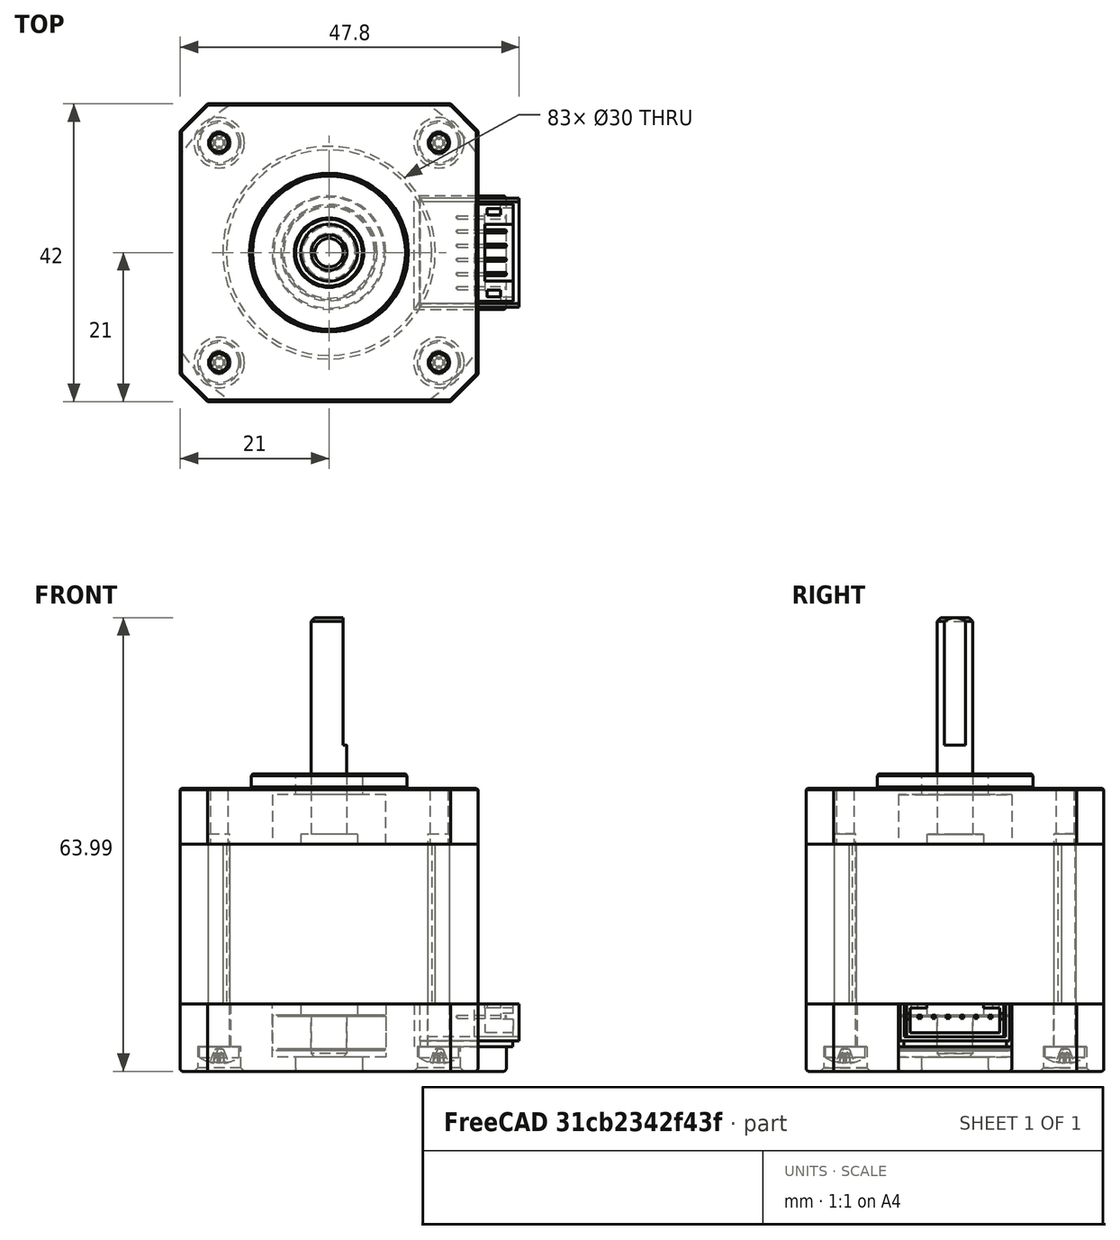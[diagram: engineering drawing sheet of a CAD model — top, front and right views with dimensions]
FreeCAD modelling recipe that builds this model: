
FCSTD DOCUMENT  (FreeCAD 0.18R16131 (Git))
Label: Nema_17-17HS4401
License: CreativeCommons Attribution
LicenseURL: http://creativecommons.org/licenses/by/4.0/
objects: Sketcher::SketchObject×21, PartDesign::Body×10, PartDesign::Pocket×10, PartDesign::Pad×8, Part::FeaturePython×5, PartDesign::Chamfer×3, PartDesign::Revolution×2, PartDesign::LinearPattern×1, PartDesign::Hole×1, PartDesign::Fillet×1, PartDesign::FeatureBase×1, App::Part×1
note: 84 computed .brp shape members not serialized (recipe doc carries the construction recipe); baked Part::Feature solids carry a one-line shape summary decoded from their .brp

FEATURE [Sketcher::SketchObject] Sketch
  MapMode = 5
  Support = -> [XY_Plane]
  sketch-geometry (1):
    g0: Circle CenterX=0 CenterY=0 CenterZ=0 NormalX=0 NormalY=0 NormalZ=1 AngleXU=0 Radius=11
  constraints (2):
    c: Coincident(g0,g-1)
    c: Diameter(g0) = 22
FEATURE [PartDesign::Pad] Pad
  Length = 2
  Length2 = 100
  Profile = -> Sketch
  Type = 0
FEATURE [Sketcher::SketchObject] Sketch001
  MapMode = 5
  Support = -> [XY_Plane]
  sketch-geometry (8):
    g0: LineSegment StartX=-21 StartY=17.15 StartZ=0 EndX=-21 EndY=-17.15 EndZ=0
    g1: LineSegment StartX=-21 StartY=-17.15 StartZ=0 EndX=-17.15 EndY=-21 EndZ=0
    g2: LineSegment StartX=-17.15 StartY=-21 StartZ=0 EndX=17.15 EndY=-21 EndZ=0
    g3: LineSegment StartX=17.15 StartY=-21 StartZ=0 EndX=21 EndY=-17.15 EndZ=0
    g4: LineSegment StartX=21 StartY=-17.15 StartZ=0 EndX=21 EndY=17.15 EndZ=0
    g5: LineSegment StartX=21 StartY=17.15 StartZ=0 EndX=17.15 EndY=21 EndZ=0
    g6: LineSegment StartX=17.15 StartY=21 StartZ=0 EndX=-17.15 EndY=21 EndZ=0
    g7: LineSegment StartX=-17.15 StartY=21 StartZ=0 EndX=-21 EndY=17.15 EndZ=0
  constraints (21):
    c: Coincident(g0,g1)
    c: Coincident(g1,g2)
    c: Coincident(g2,g3)
    c: Coincident(g3,g4)
    c: Coincident(g4,g5)
    c: Coincident(g5,g6)
    c: Coincident(g6,g7)
    c: Coincident(g7,g0)
    c: Symmetric(g1,g2,g-2)
    c: Symmetric(g0,g0,g-1)
    c: Equal(g7,g5)
    c: Equal(g5,g3)
    c: Equal(g3,g1)
    c: Equal(g0,g6)
    c: Equal(g6,g4)
    c: Equal(g4,g2)
    c: Symmetric(g6,g5,g-2)
    c: Symmetric(g4,g3,g-1)
    c: Perpendicular(g7,g1)
    c: DistanceX(g0,g4) = 42
    c: DistanceY(g2,g3) = 3.85
FEATURE [PartDesign::Pad] Pad001
  BaseFeature = -> Pad
  Length = 7.9
  Length2 = 100
  Profile = -> Sketch001
  Reversed = true
  Type = 0
FEATURE [Sketcher::SketchObject] Sketch003
  MapMode = 5
  Support = -> [XY_Plane]
  sketch-geometry (8):
    g0: LineSegment [constr] StartX=-15.5 StartY=15.5 StartZ=0 EndX=15.5 EndY=15.5 EndZ=0
    g1: LineSegment [constr] StartX=15.5 StartY=15.5 StartZ=0 EndX=15.5 EndY=-15.5 EndZ=0
    g2: LineSegment [constr] StartX=15.5 StartY=-15.5 StartZ=0 EndX=-15.5 EndY=-15.5 EndZ=0
    g3: LineSegment [constr] StartX=-15.5 StartY=-15.5 StartZ=0 EndX=-15.5 EndY=15.5 EndZ=0
    g4: Circle CenterX=-15.5 CenterY=15.5 CenterZ=0 NormalX=0 NormalY=0 NormalZ=1 AngleXU=0 Radius=1.25
    g5: Circle CenterX=15.5 CenterY=15.5 CenterZ=0 NormalX=0 NormalY=0 NormalZ=1 AngleXU=0 Radius=1.25
    g6: Circle CenterX=15.5 CenterY=-15.5 CenterZ=0 NormalX=0 NormalY=0 NormalZ=1 AngleXU=0 Radius=1.25
    g7: Circle CenterX=-15.5 CenterY=-15.5 CenterZ=0 NormalX=0 NormalY=0 NormalZ=1 AngleXU=0 Radius=1.25
  constraints (19):
    c: Coincident(g0,g1)
    c: Coincident(g1,g2)
    c: Coincident(g2,g3)
    c: Coincident(g3,g0)
    c: Horizontal(g0)
    c: Horizontal(g2)
    c: Vertical(g1)
    c: Vertical(g3)
    c: Equal(g3,g0)
    c: Symmetric(g2,g0,g-1)
    c: Coincident(g4,g0)
    c: Coincident(g5,g0)
    c: Coincident(g6,g1)
    c: Coincident(g7,g2)
    c: Equal(g4,g5)
    c: Equal(g5,g6)
    c: Equal(g6,g7)
    c: Diameter(g4) = 2.5
    c: DistanceY(g1,g1) = 31
FEATURE [Sketcher::SketchObject] Sketch004
  AttachmentOffset = pos=(0,0,-7.9) rot=(1,0,0;3.14159rad)
  MapMode = 5
  Placement = pos=(0,0,-7.9) rot=(1,0,0;3.14159rad)
  Support = -> [XY_Plane]
  expr: AttachmentOffset.Base.z = -Pad001.Length
  sketch-geometry (1):
    g0: Circle CenterX=0 CenterY=0 CenterZ=0 NormalX=0 NormalY=0 NormalZ=1 AngleXU=0 Radius=8
  constraints (2):
    c: Coincident(g0,g-1)
    c: Diameter(g0) = 16
FEATURE [Sketcher::SketchObject] Sketch005
  MapMode = 5
  Support = -> [XY_Plane001]
  sketch-geometry (25):
    g0: LineSegment StartX=-13.1381 StartY=21 StartZ=0 EndX=13.1381 EndY=21 EndZ=0
    g1: LineSegment StartX=21 StartY=13.1381 StartZ=0 EndX=21 EndY=-13.1381 EndZ=0
    g2: LineSegment StartX=13.1381 StartY=-21 StartZ=0 EndX=-13.1381 EndY=-21 EndZ=0
    g3: LineSegment StartX=-21 StartY=-13.1381 StartZ=0 EndX=-21 EndY=13.1381 EndZ=0
    g4: ArcOfCircle CenterX=-2e-16 CenterY=0 CenterZ=0 NormalX=0 NormalY=0 NormalZ=1 AngleXU=0 Radius=25.1 StartAngle=2.17578 EndAngle=2.53661
    g5: ArcOfCircle CenterX=-2e-16 CenterY=0 CenterZ=0 NormalX=0 NormalY=0 NormalZ=1 AngleXU=0 Radius=25.1 StartAngle=0.604985 EndAngle=0.965812
    g6: ArcOfCircle CenterX=-2e-16 CenterY=0 CenterZ=0 NormalX=0 NormalY=0 NormalZ=1 AngleXU=0 Radius=25.1 StartAngle=3.74658 EndAngle=4.1074
    g7: ArcOfCircle CenterX=-2e-16 CenterY=0 CenterZ=0 NormalX=0 NormalY=0 NormalZ=1 AngleXU=0 Radius=25.1 StartAngle=5.31737 EndAngle=5.6782
    g8: ArcOfCircle CenterX=-13.1381 CenterY=19 CenterZ=0 NormalX=0 NormalY=0 NormalZ=1 AngleXU=0 Radius=2 StartAngle=1.5708 EndAngle=2.17578
    g9: ArcOfCircle CenterX=13.1381 CenterY=19 CenterZ=0 NormalX=0 NormalY=0 NormalZ=1 AngleXU=0 Radius=2 StartAngle=0.965812 EndAngle=1.5708
    g10: ArcOfCircle CenterX=19 CenterY=13.1381 CenterZ=0 NormalX=0 NormalY=0 NormalZ=1 AngleXU=0 Radius=2 StartAngle=0 EndAngle=0.604985
    g11: ArcOfCircle CenterX=-19 CenterY=13.1381 CenterZ=0 NormalX=0 NormalY=0 NormalZ=1 AngleXU=0 Radius=2 StartAngle=2.53661 EndAngle=3.14159
    g12: ArcOfCircle CenterX=-19 CenterY=-13.1381 CenterZ=0 NormalX=0 NormalY=0 NormalZ=1 AngleXU=0 Radius=2 StartAngle=3.14159 EndAngle=3.74658
    g13: ArcOfCircle CenterX=-13.1381 CenterY=-19 CenterZ=0 NormalX=0 NormalY=0 NormalZ=1 AngleXU=0 Radius=2 StartAngle=4.1074 EndAngle=4.71239
    g14: ArcOfCircle CenterX=13.1381 CenterY=-19 CenterZ=0 NormalX=0 NormalY=0 NormalZ=1 AngleXU=0 Radius=2 StartAngle=4.71239 EndAngle=5.31737
    g15: ArcOfCircle CenterX=19 CenterY=-13.1381 CenterZ=0 NormalX=0 NormalY=0 NormalZ=1 AngleXU=0 Radius=2 StartAngle=5.6782 EndAngle=6.28319
    g16: Circle CenterX=-2e-16 CenterY=0 CenterZ=0 NormalX=0 NormalY=0 NormalZ=1 AngleXU=0 Radius=15
    g17: LineSegment [constr] StartX=-15.5 StartY=15.5 StartZ=0 EndX=15.5 EndY=15.5 EndZ=0
    g18: LineSegment [constr] StartX=15.5 StartY=15.5 StartZ=0 EndX=15.5 EndY=-15.5 EndZ=0
    g19: LineSegment [constr] StartX=15.5 StartY=-15.5 StartZ=0 EndX=-15.5 EndY=-15.5 EndZ=0
    g20: LineSegment [constr] StartX=-15.5 StartY=-15.5 StartZ=0 EndX=-15.5 EndY=15.5 EndZ=0
    g21: Circle CenterX=-15.5 CenterY=15.5 CenterZ=0 NormalX=0 NormalY=0 NormalZ=1 AngleXU=0 Radius=1.55
    g22: Circle CenterX=15.5 CenterY=15.5 CenterZ=0 NormalX=0 NormalY=0 NormalZ=1 AngleXU=0 Radius=1.55
    g23: Circle CenterX=15.5 CenterY=-15.5 CenterZ=0 NormalX=0 NormalY=0 NormalZ=1 AngleXU=0 Radius=1.55
    g24: Circle CenterX=-15.5 CenterY=-15.5 CenterZ=0 NormalX=0 NormalY=0 NormalZ=1 AngleXU=0 Radius=1.55
  constraints (57):
    c: Coincident(g6,g4)
    c: Coincident(g6,g5)
    c: Coincident(g6,g-1)
    c: Coincident(g7,g4)
    c: Tangent(g4,g8) = -1.5708
    c: Tangent(g0,g8) = 1.5708
    c: Tangent(g0,g9) = 1.5708
    c: Tangent(g5,g9) = -1.5708
    c: Tangent(g5,g10) = -1.5708
    c: Tangent(g1,g10) = 1.5708
    c: Tangent(g4,g11) = -1.5708
    c: Tangent(g3,g11) = 1.5708
    c: Tangent(g3,g12) = 1.5708
    c: Tangent(g6,g12) = -1.5708
    c: Tangent(g6,g13) = -1.5708
    c: Tangent(g2,g13) = 1.5708
    c: Tangent(g2,g14) = 1.5708
    c: Tangent(g7,g14) = -1.5708
    c: Tangent(g7,g15) = -1.5708
    c: Tangent(g1,g15) = 1.5708
    c: Equal(g4,g5)
    c: Equal(g5,g7)
    c: Equal(g7,g6)
    c: Equal(g11,g8)
    c: Equal(g9,g10)
    c: Equal(g15,g14)
    c: Symmetric(g12,g11,g-1)
    c: Symmetric(g10,g15,g-1)
    c: Symmetric(g8,g9,g-2)
    c: Symmetric(g13,g14,g-2)
    c: Equal(g1,g0)
    c: Equal(g0,g3)
    c: Equal(g3,g2)
    c: Radius(g7) = 25.1
    c: Radius(g15) = 2
    c: DistanceY(g2,g0) = 42
    c: Coincident(g16,g4)
    c: Diameter(g16) = 30
    c: Coincident(g17,g18)
    c: Coincident(g18,g19)
    c: Coincident(g19,g20)
    c: Coincident(g20,g17)
    c: Horizontal(g17)
    c: Horizontal(g19)
    c: Vertical(g18)
    c: Vertical(g20)
    c: Symmetric(g19,g17,g4)
    c: Equal(g20,g17)
    c: DistanceX(g17,g17) = 31
    c: Coincident(g21,g17)
    c: Coincident(g22,g17)
    c: Coincident(g23,g18)
    c: Coincident(g24,g19)
    c: Equal(g21,g22)
    c: Equal(g22,g23)
    c: Equal(g23,g24)
    c: Diameter(g24) = 3.1
FEATURE [PartDesign::Pad] Pad002
  Length = 0.525
  Length2 = 100
  Profile = -> Sketch005
  Type = 0
FEATURE [PartDesign::LinearPattern] LinearPattern
  BaseFeature = -> Pad002
  Direction = -> Sketch005 [N_Axis]
  Length = 22
  Occurrences = 43
  Originals = -> [Pad002]
FEATURE [PartDesign::Body] Body001  label="Stator"
  Group = -> [Sketch005,Pad002,LinearPattern]
  Origin = -> Origin001
  Placement = pos=(0,0,-30.425) rot=(0,0,1;0rad)
  Tip = -> LinearPattern
FEATURE [Sketcher::SketchObject] Sketch002
  MapMode = 5
  Support = -> [XY_Plane]
  sketch-geometry (1):
    g0: Circle CenterX=0 CenterY=0 CenterZ=0 NormalX=0 NormalY=0 NormalZ=1 AngleXU=0 Radius=4.7
  constraints (2):
    c: Coincident(g0,g-1)
    c: Diameter(g0) = 9.4
FEATURE [PartDesign::Pocket] Pocket
  BaseFeature = -> Pad001
  Length = 5
  Length2 = 100
  Midplane = true
  Profile = -> Sketch002
  Type = 1
FEATURE [PartDesign::Hole] Hole
  BaseFeature = -> Pocket
  Depth = 25
  DepthType = 1
  Diameter = 2.5
  DrillPoint = 1
  DrillPointAngle = 118
  HoleCutCountersinkAngle = 90
  HoleCutDepth = 0
  HoleCutDiameter = 3
  HoleCutType = 0
  ModelActualThread = false
  Profile = -> Sketch003
  Tapered = false
  TaperedAngle = 90
  ThreadAngle = 60
  ThreadClass = 0
  ThreadCutOffInner = 0.0541266
  ThreadCutOffOuter = 0.108253
  ThreadDirection = 1
  ThreadFit = 0
  ThreadPitch = 0.5
  ThreadSize = 3
  ThreadType = 1
  Threaded = true
FEATURE [PartDesign::Pocket] Pocket001
  BaseFeature = -> Hole
  Length = 7
  Length2 = 100
  Profile = -> Sketch004
  Type = 0
FEATURE [PartDesign::Chamfer] Chamfer
  Base = -> Pocket001 [Face4,Face17]
  BaseFeature = -> Pocket001
  Size = 0.2
FEATURE [PartDesign::Body] Body  label="Frontplate"
  Group = -> [Sketch,Pad,Sketch001,Pad001,Sketch002,Pocket,Sketch003,Hole,Sketch004,Pocket001,Chamfer]
  Origin = -> Origin
  Tip = -> Chamfer
FEATURE [Sketcher::SketchObject] Sketch006
  MapMode = 5
  Support = -> [XY_Plane002]
  sketch-geometry (13):
    g0: LineSegment StartX=-21 StartY=17.15 StartZ=0 EndX=-21 EndY=-17.15 EndZ=0
    g1: LineSegment StartX=-21 StartY=-17.15 StartZ=0 EndX=-17.15 EndY=-21 EndZ=0
    g2: LineSegment StartX=-17.15 StartY=-21 StartZ=0 EndX=17.15 EndY=-21 EndZ=0
    g3: LineSegment StartX=17.15 StartY=-21 StartZ=0 EndX=21 EndY=-17.15 EndZ=0
    g4: LineSegment StartX=21 StartY=17.15 StartZ=0 EndX=17.15 EndY=21 EndZ=0
    g5: LineSegment StartX=17.15 StartY=21 StartZ=0 EndX=-17.15 EndY=21 EndZ=0
    g6: LineSegment StartX=-17.15 StartY=21 StartZ=0 EndX=-21 EndY=17.15 EndZ=0
    g7: Circle CenterX=0 CenterY=0 CenterZ=0 NormalX=0 NormalY=0 NormalZ=1 AngleXU=0 Radius=4.7
    g8: LineSegment StartX=21 StartY=8 StartZ=0 EndX=25 EndY=8 EndZ=0
    g9: LineSegment StartX=25 StartY=8 StartZ=0 EndX=25 EndY=-8 EndZ=0
    g10: LineSegment StartX=25 StartY=-8 StartZ=0 EndX=21 EndY=-8 EndZ=0
    g11: LineSegment StartX=21 StartY=17.15 StartZ=0 EndX=21 EndY=8 EndZ=0
    g12: LineSegment StartX=21 StartY=-8 StartZ=0 EndX=21 EndY=-17.15 EndZ=0
  constraints (33):
    c: Coincident(g0,g1)
    c: Coincident(g1,g2)
    c: Coincident(g2,g3)
    c: Coincident(g4,g5)
    c: Coincident(g5,g6)
    c: Coincident(g6,g0)
    c: Symmetric(g1,g2,g-2)
    c: Symmetric(g0,g0,g-1)
    c: Equal(g6,g4)
    c: Equal(g4,g3)
    c: Equal(g3,g1)
    c: Equal(g0,g5)
    c: Symmetric(g5,g4,g-2)
    c: Symmetric(g4,g3,g-1)
    c: Perpendicular(g6,g1)
    c: DistanceX(g0,g4) = 42
    c: Coincident(g7,g-1)
    c: Diameter(g7) = 9.4
    c: DistanceY(g1,g0) = 3.85
    c: Horizontal(g8)
    c: Coincident(g8,g9)
    c: Coincident(g9,g10)
    c: Horizontal(g10)
    c: Symmetric(g9,g8,g-1)
    c: DistanceY(g9,g9) = 16
    c: Coincident(g11,g8)
    c: Vertical(g11)
    c: Coincident(g12,g10)
    c: Coincident(g12,g3)
    c: Vertical(g12)
    c: DistanceX(g10,g10) = 4
    c: Coincident(g4,g11)
    c: Perpendicular(g4,g6)
FEATURE [PartDesign::Pad] Pad003
  Length = 9.5
  Length2 = 100
  Profile = -> Sketch006
  Type = 0
FEATURE [Sketcher::SketchObject] Sketch007
  ExternalGeometry = -> [Sketch006]
  MapMode = 5
  Support = -> [XY_Plane002]
  sketch-geometry (4):
    g0: LineSegment StartX=12 StartY=8 StartZ=0 EndX=25 EndY=8 EndZ=0
    g1: LineSegment StartX=25 StartY=8 StartZ=0 EndX=25 EndY=-8 EndZ=0
    g2: LineSegment StartX=25 StartY=-8 StartZ=0 EndX=12 EndY=-8 EndZ=0
    g3: LineSegment StartX=12 StartY=8 StartZ=0 EndX=12 EndY=-8 EndZ=0
  constraints (10):
    c: Coincident(g0,g1)
    c: Coincident(g1,g2)
    c: Horizontal(g0)
    c: Horizontal(g2)
    c: Coincident(g1,g-4)
    c: Coincident(g0,g-3)
    c: Coincident(g3,g0)
    c: Coincident(g3,g2)
    c: Vertical(g3)
    c: DistanceX(g-1,g0) = 12
FEATURE [PartDesign::Pocket] Pocket002
  BaseFeature = -> Pad003
  Length = 6
  Length2 = 100
  Profile = -> Sketch007
  Reversed = true
  Type = 0
FEATURE [Sketcher::SketchObject] Sketch008
  MapMode = 5
  Support = -> [XY_Plane002]
  sketch-geometry (1):
    g0: Circle CenterX=0 CenterY=0 CenterZ=0 NormalX=0 NormalY=0 NormalZ=1 AngleXU=0 Radius=8
  constraints (2):
    c: Coincident(g0,g-1)
    c: Diameter(g0) = 16
FEATURE [PartDesign::Pocket] Pocket003
  BaseFeature = -> Pocket002
  Length = 7.5
  Length2 = 100
  Profile = -> Sketch008
  Reversed = true
  Type = 0
FEATURE [Sketcher::SketchObject] Sketch009
  AttachmentOffset = pos=(0,0,9.5) rot=(0,0,1;0rad)
  MapMode = 5
  Placement = pos=(0,0,9.5) rot=(0,0,1;0rad)
  Support = -> [XY_Plane002]
  expr: AttachmentOffset.Base.z = Pad003.Length
  sketch-geometry (8):
    g0: LineSegment [constr] StartX=-15.5 StartY=15.5 StartZ=0 EndX=15.5 EndY=15.5 EndZ=0
    g1: LineSegment [constr] StartX=15.5 StartY=15.5 StartZ=0 EndX=15.5 EndY=-15.5 EndZ=0
    g2: LineSegment [constr] StartX=15.5 StartY=-15.5 StartZ=0 EndX=-15.5 EndY=-15.5 EndZ=0
    g3: LineSegment [constr] StartX=-15.5 StartY=-15.5 StartZ=0 EndX=-15.5 EndY=15.5 EndZ=0
    g4: Circle CenterX=-15.5 CenterY=15.5 CenterZ=0 NormalX=0 NormalY=0 NormalZ=1 AngleXU=0 Radius=1.65
    g5: Circle CenterX=15.5 CenterY=15.5 CenterZ=0 NormalX=0 NormalY=0 NormalZ=1 AngleXU=0 Radius=1.65
    g6: Circle CenterX=15.5 CenterY=-15.5 CenterZ=0 NormalX=0 NormalY=0 NormalZ=1 AngleXU=0 Radius=1.65
    g7: Circle CenterX=-15.5 CenterY=-15.5 CenterZ=0 NormalX=0 NormalY=0 NormalZ=1 AngleXU=0 Radius=1.65
  constraints (19):
    c: Coincident(g0,g1)
    c: Coincident(g1,g2)
    c: Coincident(g2,g3)
    c: Coincident(g3,g0)
    c: Horizontal(g0)
    c: Horizontal(g2)
    c: Vertical(g1)
    c: Vertical(g3)
    c: Equal(g3,g0)
    c: Symmetric(g2,g0,g-1)
    c: DistanceX(g0,g0) = 31
    c: Coincident(g4,g0)
    c: Coincident(g5,g0)
    c: Coincident(g6,g1)
    c: Coincident(g7,g2)
    c: Equal(g4,g5)
    c: Equal(g5,g6)
    c: Equal(g6,g7)
    c: Diameter(g7) = 3.3
FEATURE [PartDesign::Pocket] Pocket004
  BaseFeature = -> Pocket003
  Length = 5
  Length2 = 100
  Profile = -> Sketch009
  Type = 1
FEATURE [Sketcher::SketchObject] Sketch010
  AttachmentOffset = pos=(0,0,9.5) rot=(0,0,1;0rad)
  MapMode = 5
  Placement = pos=(0,0,9.5) rot=(0,0,1;0rad)
  Support = -> [XY_Plane002]
  expr: Constraints[10] = Sketch009.Constraints[10]
  expr: AttachmentOffset.Base.z = Pad003.Length
  sketch-geometry (8):
    g0: LineSegment [constr] StartX=-15.5 StartY=15.5 StartZ=0 EndX=15.5 EndY=15.5 EndZ=0
    g1: LineSegment [constr] StartX=15.5 StartY=15.5 StartZ=0 EndX=15.5 EndY=-15.5 EndZ=0
    g2: LineSegment [constr] StartX=15.5 StartY=-15.5 StartZ=0 EndX=-15.5 EndY=-15.5 EndZ=0
    g3: LineSegment [constr] StartX=-15.5 StartY=-15.5 StartZ=0 EndX=-15.5 EndY=15.5 EndZ=0
    g4: Circle CenterX=-15.5 CenterY=15.5 CenterZ=0 NormalX=0 NormalY=0 NormalZ=1 AngleXU=0 Radius=3.05
    g5: Circle CenterX=15.5 CenterY=15.5 CenterZ=0 NormalX=0 NormalY=0 NormalZ=1 AngleXU=0 Radius=3.05
    g6: Circle CenterX=15.5 CenterY=-15.5 CenterZ=0 NormalX=0 NormalY=0 NormalZ=1 AngleXU=0 Radius=3.05
    g7: Circle CenterX=-15.5 CenterY=-15.5 CenterZ=0 NormalX=0 NormalY=0 NormalZ=1 AngleXU=0 Radius=3.05
  constraints (19):
    c: Coincident(g0,g1)
    c: Coincident(g1,g2)
    c: Coincident(g2,g3)
    c: Coincident(g3,g0)
    c: Horizontal(g0)
    c: Horizontal(g2)
    c: Vertical(g1)
    c: Vertical(g3)
    c: Equal(g3,g0)
    c: Symmetric(g2,g0,g-1)
    c: DistanceX(g0,g0) = 31
    c: Coincident(g4,g0)
    c: Coincident(g5,g0)
    c: Coincident(g6,g1)
    c: Coincident(g7,g2)
    c: Equal(g4,g5)
    c: Equal(g5,g6)
    c: Equal(g6,g7)
    c: Diameter(g7) = 6.1
FEATURE [PartDesign::Pocket] Pocket005
  BaseFeature = -> Pocket004
  Length = 3.5
  Length2 = 100
  Profile = -> Sketch010
  Type = 0
FEATURE [PartDesign::Fillet] Fillet
  Base = -> Pocket005 [Edge35,Edge33,Edge34,Edge32,Edge30,Edge65,Edge43,Edge26,Edge8,Edge4,Edge11,Edge27,Edge29,Edge31,Edge28]
  BaseFeature = -> Pocket005
  Radius = 0.4
FEATURE [PartDesign::Chamfer] Chamfer001
  Base = -> Fillet [Edge38,Edge40,Edge37,Edge39]
  BaseFeature = -> Fillet
  Size = 0.5
FEATURE [PartDesign::Body] Body002  label="Baseplate"
  Group = -> [Sketch006,Pad003,Sketch007,Pocket002,Sketch008,Pocket003,Sketch009,Pocket004,Sketch010,Pocket005,Fillet,Chamfer001]
  Origin = -> Origin002
  Placement = pos=(0,2e-15,-30.425) rot=(1,0,0;3.14159rad)
  Tip = -> Chamfer001
FEATURE [Sketcher::SketchObject] Sketch011
  MapMode = 5
  Placement = pos=(0,0,0) rot=(1,0,0;1.5708rad)
  Support = -> [XZ_Plane003]
  sketch-geometry (22):
    g0: LineSegment StartX=2.7 StartY=2.5 StartZ=0 EndX=3.7 EndY=2.5 EndZ=0
    g1: LineSegment StartX=8 StartY=2.3 StartZ=0 EndX=8 EndY=-2.3 EndZ=0
    g2: LineSegment StartX=7.8 StartY=-2.5 StartZ=0 EndX=6.8 EndY=-2.5 EndZ=0
    g3: LineSegment StartX=2.5 StartY=-2.3 StartZ=0 EndX=2.5 EndY=2.3 EndZ=0
    g4: LineSegment StartX=3.7 StartY=2.5 StartZ=0 EndX=3.9 EndY=2.3 EndZ=0
    g5: LineSegment StartX=3.9 StartY=2.3 StartZ=0 EndX=4.1 EndY=2.5 EndZ=0
    g6: LineSegment StartX=2.7 StartY=2.5 StartZ=0 EndX=2.5 EndY=2.3 EndZ=0
    g7: LineSegment StartX=2.5 StartY=-2.3 StartZ=0 EndX=2.7 EndY=-2.5 EndZ=0
    g8: LineSegment StartX=7.8 StartY=-2.5 StartZ=0 EndX=8 EndY=-2.3 EndZ=0
    g9: LineSegment StartX=8 StartY=2.3 StartZ=0 EndX=7.8 EndY=2.5 EndZ=0
    g10: LineSegment StartX=3.7 StartY=-2.5 StartZ=0 EndX=3.9 EndY=-2.3 EndZ=0
    g11: LineSegment StartX=3.9 StartY=-2.3 StartZ=0 EndX=4.1 EndY=-2.5 EndZ=0
    g12: LineSegment StartX=4.1 StartY=2.5 StartZ=0 EndX=6.4 EndY=2.5 EndZ=0
    g13: LineSegment StartX=3.7 StartY=-2.5 StartZ=0 EndX=2.7 EndY=-2.5 EndZ=0
    g14: LineSegment [constr] StartX=3.9 StartY=2.3 StartZ=0 EndX=3.9 EndY=-2.3 EndZ=0
    g15: LineSegment [constr] StartX=6.6 StartY=2.3 StartZ=0 EndX=6.6 EndY=-2.3 EndZ=0
    g16: LineSegment StartX=6.4 StartY=2.5 StartZ=0 EndX=6.6 EndY=2.3 EndZ=0
    g17: LineSegment StartX=6.6 StartY=2.3 StartZ=0 EndX=6.8 EndY=2.5 EndZ=0
    g18: LineSegment StartX=6.4 StartY=-2.5 StartZ=0 EndX=6.6 EndY=-2.3 EndZ=0
    g19: LineSegment StartX=6.6 StartY=-2.3 StartZ=0 EndX=6.8 EndY=-2.5 EndZ=0
    g20: LineSegment StartX=6.8 StartY=2.5 StartZ=0 EndX=7.8 EndY=2.5 EndZ=0
    g21: LineSegment StartX=6.4 StartY=-2.5 StartZ=0 EndX=4.1 EndY=-2.5 EndZ=0
  constraints (54):
    c: Coincident(g4,g5)
    c: Coincident(g11,g10)
    c: Coincident(g3,g6)
    c: Coincident(g6,g0)
    c: Coincident(g0,g4)
    c: Tangent(g0,g12)
    c: Coincident(g5,g12)
    c: Coincident(g20,g9)
    c: Coincident(g9,g1)
    c: Coincident(g2,g8)
    c: Coincident(g1,g8)
    c: Coincident(g7,g3)
    c: Coincident(g7,g13)
    c: Coincident(g13,g10)
    c: Tangent(g2,g13)
    c: Coincident(g11,g21)
    c: Equal(g7,g6)
    c: Equal(g6,g9)
    c: Equal(g9,g8)
    c: Coincident(g14,g4)
    c: Coincident(g14,g10)
    c: Symmetric(g10,g4,g-1)
    c: Symmetric(g3,g3,g-1)
    c: Symmetric(g1,g1,g-1)
    c: Equal(g1,g3)
    c: Symmetric(g0,g5,g14)
    c: Symmetric(g21,g10,g14)
    c: Symmetric(g7,g0,g-1)
    c: Perpendicular(g7,g6)
    c: DistanceY(g7,g0) = 5
    c: DistanceX(g-1,g3) = 2.5
    c: DistanceX(g-1,g1) = 8
    c: DistanceY(g14,g14) = 4.6
    c: Horizontal(g1,g4)
    c: DistanceX(g-1,g10) = 3.9
    c: Coincident(g16,g15)
    c: Coincident(g16,g17)
    c: Coincident(g18,g15)
    c: Coincident(g18,g19)
    c: Symmetric(g16,g18,g-1)
    c: Perpendicular(g19,g18)
    c: Perpendicular(g16,g17)
    c: Perpendicular(g5,g4)
    c: Perpendicular(g11,g10)
    c: Equal(g14,g15)
    c: Coincident(g12,g16)
    c: PointOnObject(g20,g17)
    c: Tangent(g12,g20)
    c: Symmetric(g17,g12,g15)
    c: Coincident(g21,g18)
    c: Tangent(g2,g21)
    c: Symmetric(g2,g18,g15)
    c: Equal(g0,g20)
    c: Coincident(g2,g19)
FEATURE [PartDesign::Revolution] Revolution
  Angle = 360
  Axis = (0,-2e-16,1)
  Base = (0,0,0)
  Placement = pos=(0,0,0) rot=(1,0,0;1.5708rad)
  Profile = -> Sketch011
  ReferenceAxis = -> Sketch011 [V_Axis]
  Reversed = true
FEATURE [PartDesign::Body] Body003  label="BallBearing1"
  Group = -> [Sketch011,Revolution]
  Origin = -> Origin003
  Placement = pos=(0,0,-4) rot=(0,0,1;0rad)
  Tip = -> Revolution
FEATURE [PartDesign::FeatureBase] Clone
  BaseFeature = -> Body003
FEATURE [PartDesign::Body] Body004  label="BallBearing2"
  BaseFeature = -> Body003
  Group = -> [Clone]
  Origin = -> Origin004
  Placement = pos=(0,0,-34.5) rot=(0,0,1;0rad)
  Tip = -> Clone
FEATURE [Sketcher::SketchObject] Sketch012
  MapMode = 5
  Placement = pos=(0,0,0) rot=(1,0,0;1.5708rad)
  Support = -> [XZ_Plane005]
  sketch-geometry (14):
    g0: LineSegment StartX=0 StartY=31 StartZ=0 EndX=0 EndY=-31 EndZ=0
    g1: LineSegment StartX=0 StartY=31 StartZ=0 EndX=2 EndY=31 EndZ=0
    g2: LineSegment StartX=2 StartY=31 StartZ=0 EndX=2.5 EndY=30.5 EndZ=0
    g3: LineSegment StartX=2.5 StartY=30.5 StartZ=0 EndX=2.5 EndY=0.425 EndZ=0
    g4: LineSegment StartX=2.5 StartY=-30.5 StartZ=0 EndX=2 EndY=-31 EndZ=0
    g5: LineSegment StartX=2 StartY=-31 StartZ=0 EndX=0 EndY=-31 EndZ=0
    g6: LineSegment StartX=2.5 StartY=0.425 StartZ=0 EndX=4 EndY=0.425 EndZ=0
    g7: LineSegment StartX=4 StartY=0.425 StartZ=0 EndX=4 EndY=-0.975 EndZ=0
    g8: LineSegment StartX=4 StartY=-0.975 StartZ=0 EndX=14.5 EndY=-0.975 EndZ=0
    g9: LineSegment StartX=14.5 StartY=-0.975 StartZ=0 EndX=14.5 EndY=-23.5 EndZ=0
    g10: LineSegment StartX=14.5 StartY=-23.5 StartZ=0 EndX=4 EndY=-23.5 EndZ=0
    g11: LineSegment StartX=4 StartY=-23.5 StartZ=0 EndX=4 EndY=-25.075 EndZ=0
    g12: LineSegment StartX=4 StartY=-25.075 StartZ=0 EndX=2.5 EndY=-25.075 EndZ=0
    g13: LineSegment StartX=2.5 StartY=-25.075 StartZ=0 EndX=2.5 EndY=-30.5 EndZ=0
  constraints (39):
    c: Symmetric(g0,g0,g-1)
    c: PointOnObject(g-1,g0)
    c: Coincident(g0,g1)
    c: Horizontal(g1)
    c: Coincident(g1,g2)
    c: Coincident(g2,g3)
    c: Coincident(g13,g4)
    c: Coincident(g4,g5)
    c: Coincident(g5,g0)
    c: DistanceY(g0,g0) = 62
    c: DistanceX(g0,g2) = 2.5
    c: Equal(g1,g5)
    c: Equal(g4,g2)
    c: Symmetric(g2,g13,g-1)
    c: Perpendicular(g2,g4)
    c: DistanceY(g2,g1) = 0.5
    c: Horizontal(g6)
    c: Coincident(g6,g7)
    c: Vertical(g7)
    c: Coincident(g7,g8)
    c: Horizontal(g8)
    c: Coincident(g8,g9)
    c: Vertical(g9)
    c: Coincident(g9,g10)
    c: Horizontal(g10)
    c: Coincident(g10,g11)
    c: Vertical(g11)
    c: Coincident(g11,g12)
    c: Horizontal(g12)
    c: Coincident(g3,g6)
    c: Coincident(g13,g12)
    c: Tangent(g3,g13)
    c: Equal(g12,g6)
    c: DistanceX(g0,g9) = 14.5
    c: DistanceX(g0,g11) = 4
    c: DistanceY(g0,g9) = 7.5
    c: DistanceY(g11,g11) = 1.575
    c: DistanceY(g7,g7) = 1.4
    c: DistanceY(g9,g9) = 22.525
FEATURE [PartDesign::Revolution] Revolution001
  Angle = 360
  Axis = (0,-2e-16,1)
  Base = (0,0,0)
  Placement = pos=(0,0,0) rot=(1,0,0;1.5708rad)
  Profile = -> Sketch012
  ReferenceAxis = -> Sketch012 [V_Axis]
  Reversed = true
FEATURE [Sketcher::SketchObject] Sketch013
  MapMode = 5
  Placement = pos=(0,0,0) rot=(1,0,0;1.5708rad)
  Support = -> [XZ_Plane005]
  sketch-geometry (4):
    g0: LineSegment StartX=2 StartY=31 StartZ=0 EndX=4 EndY=31 EndZ=0
    g1: LineSegment StartX=4 StartY=31 StartZ=0 EndX=4 EndY=13 EndZ=0
    g2: LineSegment StartX=4 StartY=13 StartZ=0 EndX=2 EndY=13 EndZ=0
    g3: LineSegment StartX=2 StartY=13 StartZ=0 EndX=2 EndY=31 EndZ=0
  constraints (12):
    c: Coincident(g0,g1)
    c: Coincident(g1,g2)
    c: Coincident(g2,g3)
    c: Coincident(g3,g0)
    c: Horizontal(g0)
    c: Horizontal(g2)
    c: Vertical(g1)
    c: Vertical(g3)
    c: DistanceX(g-1,g0) = 2
    c: DistanceX(g2,g2) = 2
    c: DistanceY(g-1,g0) = 31
    c: DistanceY(g1,g1) = 18
FEATURE [PartDesign::Pocket] Pocket006
  BaseFeature = -> Revolution001
  Length = 5
  Length2 = 100
  Midplane = true
  Placement = pos=(0,0,0) rot=(1,0,0;1.5708rad)
  Profile = -> Sketch013
  Type = 1
FEATURE [PartDesign::Body] Body005  label="Axis&Rotor"
  Group = -> [Sketch012,Revolution001,Sketch013,Pocket006]
  Origin = -> Origin005
  Placement = pos=(0,0,-6.925) rot=(0,0,1;0rad)
  Tip = -> Pocket006
FEATURE [Sketcher::SketchObject] Sketch014
  MapMode = 5
  Support = -> [XY_Plane006]
  sketch-geometry (4):
    g0: LineSegment StartX=12.9 StartY=7.25 StartZ=0 EndX=25.9 EndY=7.25 EndZ=0
    g1: LineSegment StartX=25.9 StartY=7.25 StartZ=0 EndX=25.9 EndY=-7.25 EndZ=0
    g2: LineSegment StartX=25.9 StartY=-7.25 StartZ=0 EndX=12.9 EndY=-7.25 EndZ=0
    g3: LineSegment StartX=12.9 StartY=-7.25 StartZ=0 EndX=12.9 EndY=7.25 EndZ=0
  constraints (11):
    c: Coincident(g0,g1)
    c: Coincident(g1,g2)
    c: Coincident(g2,g3)
    c: Coincident(g3,g0)
    c: Horizontal(g0)
    c: Horizontal(g2)
    c: Vertical(g3)
    c: Symmetric(g1,g0,g-1)
    c: DistanceY(g3,g3) = 14.5
    c: DistanceX(g-1,g1) = 25.9
    c: DistanceX(g2,g2) = 13
FEATURE [PartDesign::Pad] Pad004
  Length = 0.8
  Length2 = 100
  Profile = -> Sketch014
  Type = 0
FEATURE [PartDesign::Body] Body006  label="PCB"
  Group = -> [Sketch014,Pad004]
  Origin = -> Origin006
  Placement = pos=(0,0,-36.425) rot=(0,0,1;0rad)
  Tip = -> Pad004
FEATURE [Sketcher::SketchObject] Sketch015
  MapMode = 5
  Placement = pos=(0,0,0) rot=(0.57735,0.57735,0.57735;2.0944rad)
  Support = -> [YZ_Plane007]
  sketch-geometry (9):
    g0: LineSegment StartX=-7.7 StartY=5.2 StartZ=0 EndX=-7.7 EndY=0 EndZ=0
    g1: LineSegment StartX=-7.7 StartY=0 StartZ=0 EndX=7.7 EndY=0 EndZ=0
    g2: LineSegment StartX=7.7 StartY=0 StartZ=0 EndX=7.7 EndY=5.2 EndZ=0
    g3: LineSegment StartX=7.7 StartY=5.2 StartZ=0 EndX=7.16 EndY=5.2 EndZ=0
    g4: LineSegment StartX=7.16 StartY=5.2 StartZ=0 EndX=7.16 EndY=0.54 EndZ=0
    g5: LineSegment StartX=7.16 StartY=0.54 StartZ=0 EndX=-7.16 EndY=0.54 EndZ=0
    g6: LineSegment StartX=-7.16 StartY=0.54 StartZ=0 EndX=-7.16 EndY=5.2 EndZ=0
    g7: LineSegment StartX=-7.16 StartY=5.2 StartZ=0 EndX=-7.7 EndY=5.2 EndZ=0
    g8: LineSegment [constr] StartX=0 StartY=0 StartZ=0 EndX=0 EndY=0.54 EndZ=0
  constraints (26):
    c: PointOnObject(g0,g-1)
    c: Vertical(g0)
    c: Coincident(g0,g1)
    c: Coincident(g1,g2)
    c: Vertical(g2)
    c: Coincident(g2,g3)
    c: Horizontal(g3)
    c: Coincident(g3,g4)
    c: Vertical(g4)
    c: Coincident(g4,g5)
    c: Horizontal(g5)
    c: Coincident(g5,g6)
    c: Vertical(g6)
    c: Coincident(g6,g7)
    c: Coincident(g7,g0)
    c: Horizontal(g7)
    c: Equal(g7,g3)
    c: Coincident(g8,g-1)
    c: PointOnObject(g8,g5)
    c: Vertical(g8)
    c: Equal(g3,g8)
    c: Symmetric(g0,g1,g-2)
    c: Equal(g4,g6)
    c: DistanceX(g1,g1) = 15.4
    c: DistanceX(g3,g3) = 0.54
    c: DistanceY(g0,g0) = 5.2
FEATURE [PartDesign::Pad] Pad005
  Length = 14
  Length2 = 100
  Placement = pos=(0,0,0) rot=(0.57735,0.57735,0.57735;2.0944rad)
  Profile = -> Sketch015
  Type = 0
FEATURE [PartDesign::Body] Body007  label="Insulation"
  Group = -> [Sketch015,Pad005]
  Origin = -> Origin007
  Placement = pos=(26.8,-3e-15,-35.625) rot=(0,0,1;3.14159rad)
  Tip = -> Pad005
FEATURE [Sketcher::SketchObject] Sketch016
  MapMode = 5
  Support = -> [XY_Plane008]
  sketch-geometry (4):
    g0: LineSegment StartX=0 StartY=6.85 StartZ=0 EndX=-5.5 EndY=6.85 EndZ=0
    g1: LineSegment StartX=-5.5 StartY=6.85 StartZ=0 EndX=-5.5 EndY=-6.85 EndZ=0
    g2: LineSegment StartX=-5.5 StartY=-6.85 StartZ=0 EndX=0 EndY=-6.85 EndZ=0
    g3: LineSegment StartX=0 StartY=-6.85 StartZ=0 EndX=0 EndY=6.85 EndZ=0
  constraints (11):
    c: Coincident(g0,g1)
    c: Coincident(g1,g2)
    c: Coincident(g2,g3)
    c: Coincident(g3,g0)
    c: Horizontal(g0)
    c: Horizontal(g2)
    c: Vertical(g1)
    c: PointOnObject(g0,g-2)
    c: DistanceX(g2,g2) = 5.5
    c: Symmetric(g2,g0,g-1)
    c: DistanceY(g3,g3) = 13.7  'width'
FEATURE [PartDesign::Pad] Pad006
  Length = 4.6
  Length2 = 100
  Profile = -> Sketch016
  Type = 0
FEATURE [Sketcher::SketchObject] Sketch017
  MapMode = 5
  Placement = pos=(0,0,0) rot=(0.57735,0.57735,0.57735;2.0944rad)
  Support = -> [YZ_Plane008]
  expr: Constraints[18] = Pad006.Length - 1.1mm
  expr: Constraints[22] = Pad006.Length
  expr: Constraints[17] = Sketch016.Constraints.width - 1.1mm
  sketch-geometry (8):
    g0: LineSegment StartX=-4 StartY=4.6 StartZ=0 EndX=-4 EndY=4.05 EndZ=0
    g1: LineSegment StartX=-4 StartY=4.05 StartZ=0 EndX=-6.3 EndY=4.05 EndZ=0
    g2: LineSegment StartX=-6.3 StartY=4.05 StartZ=0 EndX=-6.3 EndY=0.55 EndZ=0
    g3: LineSegment StartX=-6.3 StartY=0.55 StartZ=0 EndX=6.3 EndY=0.55 EndZ=0
    g4: LineSegment StartX=6.3 StartY=0.55 StartZ=0 EndX=6.3 EndY=4.05 EndZ=0
    g5: LineSegment StartX=6.3 StartY=4.05 StartZ=0 EndX=4 EndY=4.05 EndZ=0
    g6: LineSegment StartX=4 StartY=4.05 StartZ=0 EndX=4 EndY=4.6 EndZ=0
    g7: LineSegment StartX=4 StartY=4.6 StartZ=0 EndX=-4 EndY=4.6 EndZ=0
  constraints (23):
    c: Vertical(g0)
    c: Coincident(g0,g1)
    c: Coincident(g1,g2)
    c: Vertical(g2)
    c: Coincident(g2,g3)
    c: Coincident(g3,g4)
    c: Coincident(g4,g5)
    c: Coincident(g5,g6)
    c: Vertical(g6)
    c: Coincident(g6,g7)
    c: Coincident(g7,g0)
    c: Horizontal(g7)
    c: Symmetric(g2,g3,g-2)
    c: Horizontal(g1)
    c: Horizontal(g5)
    c: Vertical(g4)
    c: Equal(g5,g1)
    c: DistanceX(g3,g3) = 12.6
    c: DistanceY(g2,g2) = 3.5
    c: DistanceY(g-1,g2) = 0.55
    c: Equal(g2,g4)
    c: DistanceX(g7,g7) = 8
    c: DistanceY(g-1,g0) = 4.6
FEATURE [PartDesign::Pocket] Pocket007
  BaseFeature = -> Pad006
  Length = 4
  Length2 = 100
  Profile = -> Sketch017
  Type = 0
FEATURE [Sketcher::SketchObject] Sketch018
  MapMode = 5
  Placement = pos=(0,0,0) rot=(0.57735,0.57735,0.57735;2.0944rad)
  Support = -> [YZ_Plane008]
  expr: Constraints[7] = Sketch016.Constraints.width
  sketch-geometry (4):
    g0: LineSegment StartX=-6.85 StartY=3.3 StartZ=0 EndX=6.85 EndY=3.3 EndZ=0
    g1: LineSegment StartX=6.85 StartY=3.3 StartZ=0 EndX=6.85 EndY=2.5 EndZ=0
    g2: LineSegment StartX=6.85 StartY=2.5 StartZ=0 EndX=-6.85 EndY=2.5 EndZ=0
    g3: LineSegment StartX=-6.85 StartY=2.5 StartZ=0 EndX=-6.85 EndY=3.3 EndZ=0
  constraints (11):
    c: Coincident(g0,g1)
    c: Coincident(g1,g2)
    c: Coincident(g2,g3)
    c: Coincident(g3,g0)
    c: Horizontal(g0)
    c: Vertical(g1)
    c: Vertical(g3)
    c: DistanceX(g2,g2) = 13.7
    c: Symmetric(g2,g1,g-2)
    c: DistanceY(g-1,g1) = 2.5
    c: DistanceY(g3,g3) = 0.8
FEATURE [PartDesign::Pocket] Pocket008
  BaseFeature = -> Pocket007
  Length = 1.8
  Length2 = 100
  Profile = -> Sketch018
  Type = 0
FEATURE [Sketcher::SketchObject] Sketch019
  AttachmentOffset = pos=(0,0,4.6) rot=(0,0,1;0rad)
  MapMode = 5
  Placement = pos=(0,0,4.6) rot=(0,0,1;0rad)
  Support = -> [XY_Plane008]
  expr: AttachmentOffset.Base.z = Pad006.Length
  sketch-geometry (9):
    g0: LineSegment StartX=-3.7 StartY=6.2 StartZ=0 EndX=-1.8 EndY=6.2 EndZ=0
    g1: LineSegment StartX=-1.8 StartY=6.2 StartZ=0 EndX=-1.8 EndY=5.3 EndZ=0
    g2: LineSegment StartX=-1.8 StartY=5.3 StartZ=0 EndX=-3.7 EndY=5.3 EndZ=0
    g3: LineSegment StartX=-3.7 StartY=5.3 StartZ=0 EndX=-3.7 EndY=6.2 EndZ=0
    g4: LineSegment StartX=-3.7 StartY=-5.3 StartZ=0 EndX=-1.8 EndY=-5.3 EndZ=0
    g5: LineSegment StartX=-1.8 StartY=-5.3 StartZ=0 EndX=-1.8 EndY=-6.2 EndZ=0
    g6: LineSegment StartX=-1.8 StartY=-6.2 StartZ=0 EndX=-3.7 EndY=-6.2 EndZ=0
    g7: LineSegment StartX=-3.7 StartY=-6.2 StartZ=0 EndX=-3.7 EndY=-5.3 EndZ=0
    g8: LineSegment [constr] StartX=-1.8 StartY=5.3 StartZ=0 EndX=-1.8 EndY=-5.3 EndZ=0
  constraints (25):
    c: Coincident(g0,g1)
    c: Coincident(g1,g2)
    c: Coincident(g2,g3)
    c: Coincident(g3,g0)
    c: Horizontal(g0)
    c: Horizontal(g2)
    c: Vertical(g1)
    c: Vertical(g3)
    c: Coincident(g4,g5)
    c: Coincident(g5,g6)
    c: Coincident(g6,g7)
    c: Coincident(g7,g4)
    c: Horizontal(g4)
    c: Horizontal(g6)
    c: Vertical(g5)
    c: Vertical(g7)
    c: Coincident(g8,g1)
    c: Coincident(g8,g4)
    c: Equal(g2,g4)
    c: Equal(g1,g5)
    c: DistanceY(g7,g7) = 0.9
    c: DistanceX(g6,g6) = 1.9
    c: DistanceX(g0,g-1) = 1.8
    c: Symmetric(g4,g1,g-1)
    c: DistanceY(g8,g8) = 10.6
FEATURE [PartDesign::Pocket] Pocket009
  BaseFeature = -> Pocket008
  Length = 1
  Length2 = 100
  Profile = -> Sketch019
  Type = 0
FEATURE [PartDesign::Body] Body008  label="ConnectrorBody"
  Group = -> [Sketch016,Pad006,Sketch017,Pocket007,Sketch018,Pocket008,Sketch019,Pocket009]
  Origin = -> Origin008
  Placement = pos=(26,0,-35.05) rot=(0,0,1;0rad)
  Tip = -> Pocket009
FEATURE [Sketcher::SketchObject] Sketch020
  MapMode = 5
  Support = -> [XY_Plane009]
  sketch-geometry (4):
    g0: LineSegment StartX=-0.225 StartY=0.225 StartZ=0 EndX=0.225 EndY=0.225 EndZ=0
    g1: LineSegment StartX=0.225 StartY=0.225 StartZ=0 EndX=0.225 EndY=-0.225 EndZ=0
    g2: LineSegment StartX=0.225 StartY=-0.225 StartZ=0 EndX=-0.225 EndY=-0.225 EndZ=0
    g3: LineSegment StartX=-0.225 StartY=-0.225 StartZ=0 EndX=-0.225 EndY=0.225 EndZ=0
  constraints (11):
    c: Coincident(g0,g1)
    c: Coincident(g1,g2)
    c: Coincident(g2,g3)
    c: Coincident(g3,g0)
    c: Horizontal(g0)
    c: Horizontal(g2)
    c: Vertical(g1)
    c: Vertical(g3)
    c: Equal(g0,g3)
    c: Symmetric(g0,g2,g-1)
    c: DistanceY(g3,g3) = 0.45
FEATURE [PartDesign::Pad] Pad007
  Length = 7
  Length2 = 100
  Profile = -> Sketch020
  Type = 0
FEATURE [PartDesign::Chamfer] Chamfer002
  Base = -> Pad007 [Face5,Face6]
  BaseFeature = -> Pad007
  Size = 0.12
FEATURE [PartDesign::Body] Body009  label="ConnectorPin"
  Group = -> [Sketch020,Pad007,Chamfer002]
  Origin = -> Origin009
  Tip = -> Chamfer002
FEATURE [Part::FeaturePython] Array  label="ConnectorPins"  # Draft array (typed FeaturePython)
  Angle = 360
  ArrayType = 0
  Axis = (0,0,1)
  Base = -> Body009
  Center = (0,0,0)
  Fuse = false
  IntervalAxis = (0,0,0)
  IntervalX = (2,0,0)
  IntervalY = (0,0,0)
  IntervalZ = (0,0,0)
  NumberPolar = 1
  NumberX = 6
  NumberY = 1
  NumberZ = 1
  Placement = pos=(18,-5,-32.225) rot=(0.57735,0.57735,0.57735;2.0944rad)
FEATURE [Part::FeaturePython] Screw  label="M3x30-Screw_001"  # Fasteners workbench fastener (typed FeaturePython)
  Placement = pos=(15.5,15.5,-36.425) rot=(0,1,0;3.14159rad)
  diameter = 4
  invert = false
  length = 10
  matchOuter = false
  offset = 0
  thread = false
  type = 16
FEATURE [Part::FeaturePython] Screw001  label="M3x30-Screw_002"  # Fasteners workbench fastener (typed FeaturePython)
  Placement = pos=(-15.5,15.5,-36.425) rot=(0,1,0;3.14159rad)
  diameter = 4
  invert = false
  length = 10
  matchOuter = false
  offset = 0
  thread = false
  type = 16
FEATURE [Part::FeaturePython] Screw002  label="M3x30-Screw_003"  # Fasteners workbench fastener (typed FeaturePython)
  Placement = pos=(15.5,-15.5,-36.425) rot=(0,1,0;3.14159rad)
  diameter = 4
  invert = false
  length = 10
  matchOuter = false
  offset = 0
  thread = false
  type = 16
FEATURE [Part::FeaturePython] Screw003  label="M3x30-Screw_004"  # Fasteners workbench fastener (typed FeaturePython)
  Placement = pos=(-15.5,-15.5,-36.425) rot=(0,1,0;3.14159rad)
  diameter = 4
  invert = false
  length = 10
  matchOuter = false
  offset = 0
  thread = false
  type = 16
FEATURE [App::Part] Part  label="Screws"
  Group = -> [Screw,Screw001,Screw002,Screw003]
  Origin = -> Origin010
